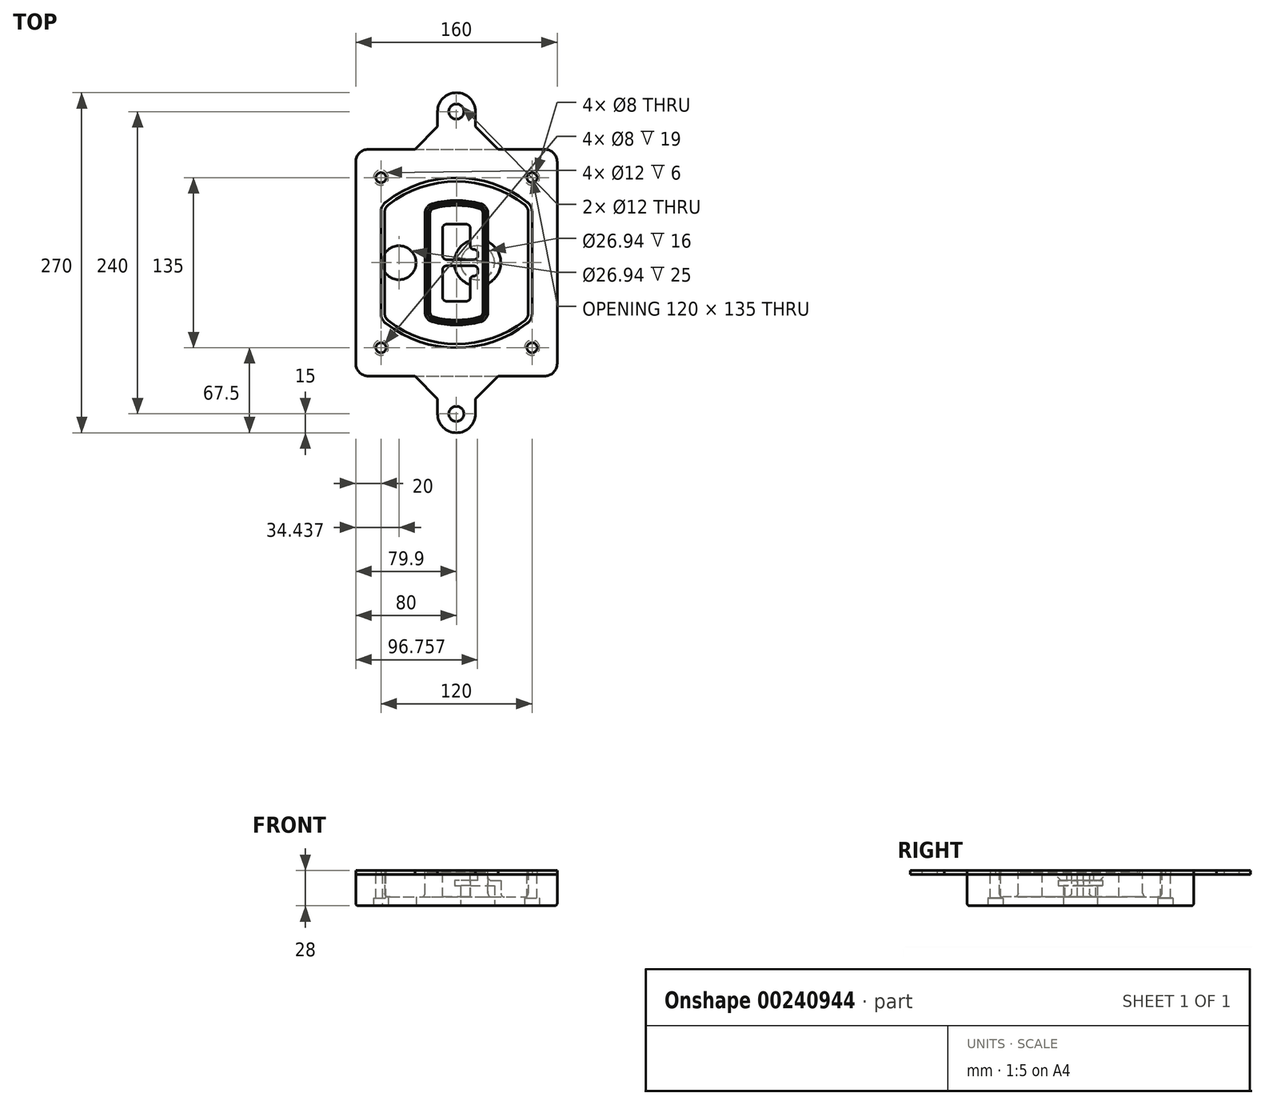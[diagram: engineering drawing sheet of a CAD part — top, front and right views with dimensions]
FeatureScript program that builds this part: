
annotation { "Feature Type Name" : "Feature", "Feature Type Description" : "" }
export const myFeature = defineFeature(function(context is Context, id is Id, definition is map)
    precondition{}
    {
        {
            var Q0;
            Q0=qCreatedBy(makeId("Top.planeOp"),FACE);
            var sketch = newSketch(context, id + "F0", { "sketchPlane" : qUnion([Q0])});
            skPoint(sketch, "E0.rect.middle", {"position": v(0, 0) * mm});
            skLineSegment(sketch, "E1.bottom", {"start": v(-70, -90) * mm, "end": v(70, -90) * mm});
            skLineSegment(sketch, "E1.top", {"start": v(-70, 90) * mm, "end": v(70, 90) * mm});
            skLineSegment(sketch, "E1.left", {"start": v(-80, -80) * mm, "end": v(-80, 80) * mm});
            skLineSegment(sketch, "E1.right", {"start": v(80, -80) * mm, "end": v(80, 80) * mm});
            skLineSegment(sketch, "E2", {"start": v(-80, 90) * mm, "end": v(80, -90) * mm, "construction": true});
            skLineSegment(sketch, "E3", {"start": v(80, 90) * mm, "end": v(-80, -90) * mm, "construction": true});
            skCircle(sketch, "E4", {"center": v(-60, 67.5) * mm, "radius": 4 * mm});
            skCircle(sketch, "E5", {"center": v(60, 67.5) * mm, "radius": 4 * mm});
            skCircle(sketch, "E6", {"center": v(60, -67.5) * mm, "radius": 4 * mm});
            skCircle(sketch, "E7", {"center": v(-60, -67.5) * mm, "radius": 4 * mm});
            skLineSegment(sketch, "E8", {"start": v(-60, 67.5) * mm, "end": v(60, 67.5) * mm, "construction": true});
            skLineSegment(sketch, "E9", {"start": v(60, 67.5) * mm, "end": v(60, -67.5) * mm, "construction": true});
            skLineSegment(sketch, "E10", {"start": v(60, -67.5) * mm, "end": v(-60, -67.5) * mm, "construction": true});
            skLineSegment(sketch, "E11", {"start": v(-60, -67.5) * mm, "end": v(-60, 67.5) * mm, "construction": true});
            skLineSegment(sketch, "E12", {"start": v(-60, 40.3) * mm, "end": v(-60, -40.3) * mm});
            skLineSegment(sketch, "E13", {"start": v(60, 40.3) * mm, "end": v(60, -40.3) * mm});
            skArc(sketch, "E14", {"start": v(56.15, 48.18) * mm, "mid": v(0, 67.5) * mm, "end": v(-56.15, 48.18) * mm});
            skArc(sketch, "E15", {"start": v(-56.15, -48.18) * mm, "mid": v(0, -67.5) * mm, "end": v(56.15, -48.18) * mm});
            skLineSegment(sketch, "E16", {"start": v(-60, 0) * mm, "end": v(60, 0) * mm, "construction": true});
            skPoint(sketch, "E17.visualSharp", {"position": v(-60, -45) * mm});
            skArc(sketch, "E17.filletArc", {"start": v(-60, -40.3) * mm, "mid": v(-58.99, -44.68) * mm, "end": v(-56.15, -48.18) * mm});
            skPoint(sketch, "E18.visualSharp", {"position": v(-60, 45) * mm});
            skArc(sketch, "E18.filletArc", {"start": v(-56.15, 48.18) * mm, "mid": v(-58.99, 44.68) * mm, "end": v(-60, 40.3) * mm});
            skPoint(sketch, "E19.visualSharp", {"position": v(60, 45) * mm});
            skArc(sketch, "E19.filletArc", {"start": v(60, 40.3) * mm, "mid": v(58.99, 44.68) * mm, "end": v(56.15, 48.18) * mm});
            skPoint(sketch, "E20.visualSharp", {"position": v(60, -45) * mm});
            skArc(sketch, "E20.filletArc", {"start": v(56.15, -48.18) * mm, "mid": v(58.99, -44.68) * mm, "end": v(60, -40.3) * mm});
            skPoint(sketch, "E21.visualSharp", {"position": v(-80, 90) * mm});
            skArc(sketch, "E21.filletArc", {"start": v(-70, 90) * mm, "mid": v(-77.07, 87.07) * mm, "end": v(-80, 80) * mm});
            skPoint(sketch, "E22.visualSharp", {"position": v(80, 90) * mm});
            skArc(sketch, "E22.filletArc", {"start": v(80, 80) * mm, "mid": v(77.07, 87.07) * mm, "end": v(70, 90) * mm});
            skPoint(sketch, "E23.visualSharp", {"position": v(80, -90) * mm});
            skArc(sketch, "E23.filletArc", {"start": v(70, -90) * mm, "mid": v(77.07, -87.07) * mm, "end": v(80, -80) * mm});
            skPoint(sketch, "E24.visualSharp", {"position": v(-80, -90) * mm});
            skArc(sketch, "E24.filletArc", {"start": v(-80, -80) * mm, "mid": v(-77.07, -87.07) * mm, "end": v(-70, -90) * mm});
            skArc(sketch, "E25.0", {"start": v(57, 40.3) * mm, "mid": v(56.3, 43.36) * mm, "end": v(54.3, 45.81) * mm});
            skLineSegment(sketch, "E25.1", {"start": v(57, 40.3) * mm, "end": v(57, -40.3) * mm});
            skArc(sketch, "E25.2", {"start": v(54.3, -45.81) * mm, "mid": v(56.3, -43.36) * mm, "end": v(57, -40.3) * mm});
            skArc(sketch, "E25.3", {"start": v(-54.3, -45.81) * mm, "mid": v(0, -64.5) * mm, "end": v(54.3, -45.81) * mm});
            skArc(sketch, "E25.4", {"start": v(-57, -40.3) * mm, "mid": v(-56.3, -43.36) * mm, "end": v(-54.3, -45.81) * mm});
            skArc(sketch, "E25.5", {"start": v(54.3, 45.81) * mm, "mid": v(0, 64.5) * mm, "end": v(-54.3, 45.81) * mm});
            skLineSegment(sketch, "E25.6", {"start": v(-57, 40.3) * mm, "end": v(-57, -40.3) * mm});
            skArc(sketch, "E25.7", {"start": v(-54.3, 45.81) * mm, "mid": v(-56.3, 43.36) * mm, "end": v(-57, 40.3) * mm});
            skArc(sketch, "E26.0", {"start": v(-58.62, 51.33) * mm, "mid": v(-62.58, 46.43) * mm, "end": v(-64, 40.3) * mm});
            skArc(sketch, "E26.1", {"start": v(58.62, 51.33) * mm, "mid": v(0, 71.5) * mm, "end": v(-58.62, 51.33) * mm});
            skArc(sketch, "E26.2", {"start": v(64, 40.3) * mm, "mid": v(62.58, 46.43) * mm, "end": v(58.62, 51.33) * mm});
            skLineSegment(sketch, "E26.3", {"start": v(64, 40.3) * mm, "end": v(64, -40.3) * mm});
            skArc(sketch, "E26.4", {"start": v(58.62, -51.33) * mm, "mid": v(62.58, -46.43) * mm, "end": v(64, -40.3) * mm});
            skLineSegment(sketch, "E26.5", {"start": v(-64, 40.3) * mm, "end": v(-64, -40.3) * mm});
            skArc(sketch, "E26.6", {"start": v(-58.62, -51.33) * mm, "mid": v(0, -71.5) * mm, "end": v(58.62, -51.33) * mm});
            skArc(sketch, "E26.7", {"start": v(-64, -40.3) * mm, "mid": v(-62.58, -46.43) * mm, "end": v(-58.62, -51.33) * mm});
            skSolve(sketch);
        }
        {
            var Q0;
            Q0=makeQuery(id+"F0.imprint","IMPRINT",FACE,{"disambiguationData":[TD([[makeQuery(id+"F0.imprint","IMPRINT",EDGE,{"derivedFrom":sQuery(id+"F0.wireOp",EDGE,"E1.bottom")}),1.0]])]});
            var Q1;
            Q1=makeQuery(id+"F0.imprint","IMPRINT",FACE,{"disambiguationData":[TD([[makeQuery(id+"F0.imprint","IMPRINT",EDGE,{"derivedFrom":sQuery(id+"F0.wireOp",EDGE,"E12")}),1.0]])]});
            var Q2;
            Q2=makeQuery(id+"F0.imprint","IMPRINT",FACE,{"disambiguationData":[TD([[makeQuery(id+"F0.imprint","IMPRINT",EDGE,{"derivedFrom":sQuery(id+"F0.wireOp",EDGE,"E25.0")}),1.0]])]});
            var Q3;
            Q3=makeQuery(id+"F0.imprint","IMPRINT",FACE,{"disambiguationData":[TD([[makeQuery(id+"F0.imprint","IMPRINT",EDGE,{"derivedFrom":sQuery(id+"F0.wireOp",EDGE,"E12")}),-1.0]])]});
            extrude(context, id + "F1", {"entities" : qUnion([Q0, Q1, Q2, Q3]), "oppositeDirection" : true, "depth" : 25 * mm});
        }
        {
            var Q0;
            Q0=makeQuery(id+"F0.imprint","IMPRINT",FACE,{"disambiguationData":[TD([[makeQuery(id+"F0.imprint","IMPRINT",EDGE,{"derivedFrom":sQuery(id+"F0.wireOp",EDGE,"E12")}),1.0]])]});
            extrude(context, id + "F2", {"entities" : qUnion([Q0]), "operationType" : NewBodyOperationType.ADD, "depth" : 3 * mm});
        }
        {
            var Q0;
            Q0=makeQuery(id+"F0.imprint","IMPRINT",FACE,{"disambiguationData":[TD([[makeQuery(id+"F0.imprint","IMPRINT",EDGE,{"derivedFrom":sQuery(id+"F0.wireOp",EDGE,"E25.0")}),1.0]])]});
            extrude(context, id + "F3", {"entities" : qUnion([Q0]), "operationType" : NewBodyOperationType.REMOVE, "oppositeDirection" : true, "depth" : 18 * mm});
        }
        {
            var Q0;
            Q0=makeQuery(id+"F2.opExtrude","CAP_FACE",FACE,{"disambiguationData":[OSD([sQuery(id+"F0.wireOp",EDGE,"E12"),sQuery(id+"F0.wireOp",EDGE,"E13"),sQuery(id+"F0.wireOp",EDGE,"E14"),sQuery(id+"F0.wireOp",EDGE,"E15"),sQuery(id+"F0.wireOp",EDGE,"E17.filletArc"),sQuery(id+"F0.wireOp",EDGE,"E18.filletArc"),sQuery(id+"F0.wireOp",EDGE,"E19.filletArc"),sQuery(id+"F0.wireOp",EDGE,"E20.filletArc"),sQuery(id+"F0.wireOp",EDGE,"E25.0"),sQuery(id+"F0.wireOp",EDGE,"E25.1"),sQuery(id+"F0.wireOp",EDGE,"E25.2"),sQuery(id+"F0.wireOp",EDGE,"E25.3"),sQuery(id+"F0.wireOp",EDGE,"E25.4"),sQuery(id+"F0.wireOp",EDGE,"E25.5"),sQuery(id+"F0.wireOp",EDGE,"E25.6"),sQuery(id+"F0.wireOp",EDGE,"E25.7")])],"isStart":false});
            var sketch = newSketch(context, id + "F4", { "sketchPlane" : qUnion([Q0])});
            skArc(sketch, "E27.0", {"start": v(-19.08, -46.97) * mm, "mid": v(0, -49.5) * mm, "end": v(19.08, -46.97) * mm});
            skArc(sketch, "E28.0", {"start": v(19.08, 46.97) * mm, "mid": v(0, 49.5) * mm, "end": v(-19.08, 46.97) * mm});
            skLineSegment(sketch, "E29", {"start": v(-25, 39.25) * mm, "end": v(-25, -39.25) * mm});
            skLineSegment(sketch, "E30", {"start": v(25, 39.25) * mm, "end": v(25, -39.25) * mm});
            skLineSegment(sketch, "E31", {"start": v(-25, 45.1) * mm, "end": v(25, 45.1) * mm, "construction": true});
            skLineSegment(sketch, "E32", {"start": v(-25, -45.1) * mm, "end": v(25, -45.1) * mm, "construction": true});
            skPoint(sketch, "E33.visualSharp", {"position": v(-25, 45.1) * mm});
            skArc(sketch, "E33.filletArc", {"start": v(-19.08, 46.97) * mm, "mid": v(-23.35, 44.11) * mm, "end": v(-25, 39.25) * mm});
            skPoint(sketch, "E34.visualSharp", {"position": v(25, 45.1) * mm});
            skArc(sketch, "E34.filletArc", {"start": v(25, 39.25) * mm, "mid": v(23.35, 44.11) * mm, "end": v(19.08, 46.97) * mm});
            skPoint(sketch, "E35.visualSharp", {"position": v(25, -45.1) * mm});
            skArc(sketch, "E35.filletArc", {"start": v(19.08, -46.97) * mm, "mid": v(23.35, -44.11) * mm, "end": v(25, -39.25) * mm});
            skPoint(sketch, "E36.visualSharp", {"position": v(-25, -45.1) * mm});
            skArc(sketch, "E36.filletArc", {"start": v(-25, -39.25) * mm, "mid": v(-23.35, -44.11) * mm, "end": v(-19.08, -46.97) * mm});
            skArc(sketch, "E37.0", {"start": v(54.3, 45.81) * mm, "mid": v(0, 64.5) * mm, "end": v(-54.3, 45.81) * mm});
            skArc(sketch, "E37.1", {"start": v(-54.3, 45.81) * mm, "mid": v(-56.3, 43.36) * mm, "end": v(-57, 40.3) * mm});
            skLineSegment(sketch, "E37.2", {"start": v(-57, 40.3) * mm, "end": v(-57, -40.3) * mm});
            skArc(sketch, "E37.3", {"start": v(-57, -40.3) * mm, "mid": v(-56.3, -43.36) * mm, "end": v(-54.3, -45.81) * mm});
            skArc(sketch, "E37.4", {"start": v(-54.3, -45.81) * mm, "mid": v(0, -64.5) * mm, "end": v(54.3, -45.81) * mm});
            skArc(sketch, "E37.5", {"start": v(54.3, -45.81) * mm, "mid": v(56.3, -43.36) * mm, "end": v(57, -40.3) * mm});
            skLineSegment(sketch, "E37.6", {"start": v(57, 40.3) * mm, "end": v(57, -40.3) * mm});
            skArc(sketch, "E37.7", {"start": v(57, 40.3) * mm, "mid": v(56.3, 43.36) * mm, "end": v(54.3, 45.81) * mm});
            skLineSegment(sketch, "E38.0", {"start": v(23, 39.25) * mm, "end": v(23, -39.25) * mm});
            skArc(sketch, "E38.1", {"start": v(18.56, -45.04) * mm, "mid": v(21.76, -42.9) * mm, "end": v(23, -39.25) * mm});
            skArc(sketch, "E38.2", {"start": v(-18.56, -45.04) * mm, "mid": v(0, -47.5) * mm, "end": v(18.56, -45.04) * mm});
            skArc(sketch, "E38.3", {"start": v(-23, -39.25) * mm, "mid": v(-21.76, -42.9) * mm, "end": v(-18.56, -45.04) * mm});
            skLineSegment(sketch, "E38.4", {"start": v(-23, 39.25) * mm, "end": v(-23, -39.25) * mm});
            skArc(sketch, "E38.5", {"start": v(23, 39.25) * mm, "mid": v(21.76, 42.9) * mm, "end": v(18.56, 45.04) * mm});
            skArc(sketch, "E38.6", {"start": v(-18.56, 45.04) * mm, "mid": v(-21.76, 42.9) * mm, "end": v(-23, 39.25) * mm});
            skArc(sketch, "E38.7", {"start": v(18.56, 45.04) * mm, "mid": v(0, 47.5) * mm, "end": v(-18.56, 45.04) * mm});
            skArc(sketch, "E39.0", {"start": v(21, 39.25) * mm, "mid": v(20.18, 41.68) * mm, "end": v(18.04, 43.1) * mm});
            skLineSegment(sketch, "E39.1", {"start": v(21, 39.25) * mm, "end": v(21, -39.25) * mm});
            skArc(sketch, "E39.2", {"start": v(18.04, -43.1) * mm, "mid": v(20.18, -41.68) * mm, "end": v(21, -39.25) * mm});
            skArc(sketch, "E39.3", {"start": v(-18.04, -43.1) * mm, "mid": v(0, -45.5) * mm, "end": v(18.04, -43.1) * mm});
            skArc(sketch, "E39.4", {"start": v(-21, -39.25) * mm, "mid": v(-20.18, -41.68) * mm, "end": v(-18.04, -43.1) * mm});
            skArc(sketch, "E39.5", {"start": v(18.04, 43.1) * mm, "mid": v(0, 45.5) * mm, "end": v(-18.04, 43.1) * mm});
            skLineSegment(sketch, "E39.6", {"start": v(-21, 39.25) * mm, "end": v(-21, -39.25) * mm});
            skArc(sketch, "E39.7", {"start": v(-18.04, 43.1) * mm, "mid": v(-20.18, 41.68) * mm, "end": v(-21, 39.25) * mm});
            skLineSegment(sketch, "E40", {"start": v(-25, 0) * mm, "end": v(25, 0) * mm, "construction": true});
            skLineSegment(sketch, "E41", {"start": v(-11, 5.5) * mm, "end": v(-11, 27.5) * mm});
            skLineSegment(sketch, "E42", {"start": v(-8, 30.5) * mm, "end": v(8, 30.5) * mm});
            skLineSegment(sketch, "E43", {"start": v(11, 27.5) * mm, "end": v(11, 13.5) * mm});
            skLineSegment(sketch, "E44", {"start": v(14, 10.5) * mm, "end": v(14, 10.5) * mm});
            skLineSegment(sketch, "E45", {"start": v(17, 7.5) * mm, "end": v(17, 5.5) * mm});
            skLineSegment(sketch, "E46", {"start": v(14, 2.5) * mm, "end": v(-8, 2.5) * mm});
            skPoint(sketch, "E47.visualSharp", {"position": v(-11, 30.5) * mm});
            skArc(sketch, "E47.filletArc", {"start": v(-8, 30.5) * mm, "mid": v(-10.12, 29.62) * mm, "end": v(-11, 27.5) * mm});
            skPoint(sketch, "E48.visualSharp", {"position": v(11, 30.5) * mm});
            skArc(sketch, "E48.filletArc", {"start": v(11, 27.5) * mm, "mid": v(10.12, 29.62) * mm, "end": v(8, 30.5) * mm});
            skPoint(sketch, "E49.visualSharp", {"position": v(11, 10.5) * mm});
            skArc(sketch, "E49.filletArc", {"start": v(11, 13.5) * mm, "mid": v(11.88, 11.38) * mm, "end": v(14, 10.5) * mm});
            skPoint(sketch, "E50.visualSharp", {"position": v(17, 10.5) * mm});
            skArc(sketch, "E50.filletArc", {"start": v(17, 7.5) * mm, "mid": v(16.12, 9.62) * mm, "end": v(14, 10.5) * mm});
            skPoint(sketch, "E51.visualSharp", {"position": v(17, 2.5) * mm});
            skArc(sketch, "E51.filletArc", {"start": v(14, 2.5) * mm, "mid": v(16.12, 3.38) * mm, "end": v(17, 5.5) * mm});
            skPoint(sketch, "E52.visualSharp", {"position": v(-11, 2.5) * mm});
            skArc(sketch, "E52.filletArc", {"start": v(-11, 5.5) * mm, "mid": v(-10.12, 3.38) * mm, "end": v(-8, 2.5) * mm});
            skLineSegment(sketch, "E53.0.MirrorCS", {"start": v(14, -2.5) * mm, "end": v(-8, -2.5) * mm});
            skArc(sketch, "E54.0.MirrorCS", {"start": v(-11, -5.5) * mm, "mid": v(-10.12, -3.38) * mm, "end": v(-8, -2.5) * mm});
            skLineSegment(sketch, "E55.0.MirrorCS", {"start": v(-11, -5.5) * mm, "end": v(-11, -27.5) * mm});
            skArc(sketch, "E56.0.MirrorCS", {"start": v(-8, -30.5) * mm, "mid": v(-10.12, -29.62) * mm, "end": v(-11, -27.5) * mm});
            skLineSegment(sketch, "E57.0.MirrorCS", {"start": v(-8, -30.5) * mm, "end": v(8, -30.5) * mm});
            skArc(sketch, "E58.0.MirrorCS", {"start": v(11, -27.5) * mm, "mid": v(10.12, -29.62) * mm, "end": v(8, -30.5) * mm});
            skLineSegment(sketch, "E59.0.MirrorCS", {"start": v(11, -27.5) * mm, "end": v(11, -13.5) * mm});
            skArc(sketch, "E60.0.MirrorCS", {"start": v(11, -13.5) * mm, "mid": v(11.88, -11.38) * mm, "end": v(14, -10.5) * mm});
            skArc(sketch, "E61.0.MirrorCS", {"start": v(17, -7.5) * mm, "mid": v(16.12, -9.62) * mm, "end": v(14, -10.5) * mm});
            skLineSegment(sketch, "E62.0.MirrorCS", {"start": v(17, -7.5) * mm, "end": v(17, -5.5) * mm});
            skArc(sketch, "E63.0.MirrorCS", {"start": v(14, -2.5) * mm, "mid": v(16.12, -3.38) * mm, "end": v(17, -5.5) * mm});
            skSolve(sketch);
        }
        {
            var Q0;
            Q0=makeQuery(id+"F4.imprint","IMPRINT",FACE,{"disambiguationData":[TD([[makeQuery(id+"F4.imprint","IMPRINT",EDGE,{"derivedFrom":sQuery(id+"F4.wireOp",EDGE,"E27.0")}),1.0]])]});
            var Q1;
            Q1=makeQuery(id+"F4.imprint","IMPRINT",FACE,{"disambiguationData":[TD([[makeQuery(id+"F4.imprint","IMPRINT",EDGE,{"derivedFrom":sQuery(id+"F4.wireOp",EDGE,"E38.0")}),-1.0]])]});
            var Q2;
            Q2=makeQuery(id+"F4.imprint","IMPRINT",FACE,{"disambiguationData":[TD([[makeQuery(id+"F4.imprint","IMPRINT",EDGE,{"derivedFrom":sQuery(id+"F4.wireOp",EDGE,"E39.0")}),1.0]])]});
            extrude(context, id + "F5", {"entities" : qUnion([Q0, Q1, Q2]), "operationType" : NewBodyOperationType.ADD, "endBound" : BoundingType.UP_TO_NEXT, "oppositeDirection" : true, "depth" : 25 * mm});
        }
        {
            var Q0;
            Q0=makeQuery(id+"F4.imprint","IMPRINT",FACE,{"disambiguationData":[TD([[makeQuery(id+"F4.imprint","IMPRINT",EDGE,{"derivedFrom":sQuery(id+"F4.wireOp",EDGE,"E38.0")}),-1.0]])]});
            extrude(context, id + "F6", {"entities" : qUnion([Q0]), "operationType" : NewBodyOperationType.REMOVE, "oppositeDirection" : true, "depth" : 2 * mm});
        }
        {
            var Q0;
            Q0=makeQuery(id+"F1.opExtrude","CAP_FACE",FACE,{"disambiguationData":[OSD([sQuery(id+"F0.wireOp",EDGE,"E1.bottom"),sQuery(id+"F0.wireOp",EDGE,"E1.top"),sQuery(id+"F0.wireOp",EDGE,"E1.left"),sQuery(id+"F0.wireOp",EDGE,"E1.right"),sQuery(id+"F0.wireOp",EDGE,"E4"),sQuery(id+"F0.wireOp",EDGE,"E5"),sQuery(id+"F0.wireOp",EDGE,"E6"),sQuery(id+"F0.wireOp",EDGE,"E7"),sQuery(id+"F0.wireOp",EDGE,"E21.filletArc"),sQuery(id+"F0.wireOp",EDGE,"E22.filletArc"),sQuery(id+"F0.wireOp",EDGE,"E23.filletArc"),sQuery(id+"F0.wireOp",EDGE,"E24.filletArc")])],"isStart":false});
            var sketch = newSketch(context, id + "F7", { "sketchPlane" : qUnion([Q0])});
            skCircle(sketch, "E64", {"center": v(16.76, 0) * mm, "radius": 13.47 * mm});
            skCircle(sketch, "E65", {"center": v(-45.56, 0) * mm, "radius": 13.47 * mm});
            skLineSegment(sketch, "E66", {"start": v(80, 0) * mm, "end": v(-80, 0) * mm});
            skCircle(sketch, "E67", {"center": v(16.76, 0) * mm, "radius": 18.47 * mm});
            skCircle(sketch, "E68", {"center": v(60, -67.5) * mm, "radius": 6 * mm});
            skCircle(sketch, "E69", {"center": v(-60, -67.5) * mm, "radius": 6 * mm});
            skCircle(sketch, "E70", {"center": v(-60, 67.5) * mm, "radius": 6 * mm});
            skCircle(sketch, "E71", {"center": v(60, 67.5) * mm, "radius": 6 * mm});
            skSolve(sketch);
        }
        {
            var Q0;
            {var subQ1=sQuery(id+"F7.wireOp",EDGE,"E66");var subQ4=sQuery(id+"F7.wireOp",EDGE,"E64");var subQ6=makeQuery(id+"F7.imprint","INTERSECT",VERTEX,{"disambiguationData":[OD(0.0)],"derivedFrom":[subQ4,subQ1]});Q0=makeQuery(id+"F7.imprint","IMPRINT",FACE,{"disambiguationData":[TD([[makeQuery(id+"F7.imprint","IMPRINT",EDGE,{"disambiguationData":[TD([[subQ6,-1.0]])],"derivedFrom":subQ4}),-1.0]])]});}
            var Q1;
            {var subQ0=sQuery(id+"F7.wireOp",EDGE,"E66");var subQ1=sQuery(id+"F7.wireOp",EDGE,"E64");var subQ3=makeQuery(id+"F7.imprint","INTERSECT",VERTEX,{"disambiguationData":[OD(0.0)],"derivedFrom":[subQ1,subQ0]});Q1=makeQuery(id+"F7.imprint","IMPRINT",FACE,{"disambiguationData":[TD([[makeQuery(id+"F7.imprint","IMPRINT",EDGE,{"disambiguationData":[TD([[subQ3,-1.0]])],"derivedFrom":subQ1}),1.0]])]});}
            var Q2;
            {var subQ0=sQuery(id+"F7.wireOp",EDGE,"E66");var subQ1=sQuery(id+"F7.wireOp",EDGE,"E64");var subQ3=makeQuery(id+"F7.imprint","INTERSECT",VERTEX,{"disambiguationData":[OD(0.0)],"derivedFrom":[subQ1,subQ0]});Q2=makeQuery(id+"F7.imprint","IMPRINT",FACE,{"disambiguationData":[TD([[makeQuery(id+"F7.imprint","IMPRINT",EDGE,{"disambiguationData":[TD([[subQ3,1.0]])],"derivedFrom":subQ1}),1.0]])]});}
            var Q3;
            {var subQ1=sQuery(id+"F7.wireOp",EDGE,"E66");var subQ4=sQuery(id+"F7.wireOp",EDGE,"E64");var subQ6=makeQuery(id+"F7.imprint","INTERSECT",VERTEX,{"disambiguationData":[OD(0.0)],"derivedFrom":[subQ4,subQ1]});Q3=makeQuery(id+"F7.imprint","IMPRINT",FACE,{"disambiguationData":[TD([[makeQuery(id+"F7.imprint","IMPRINT",EDGE,{"disambiguationData":[TD([[subQ6,1.0]])],"derivedFrom":subQ4}),-1.0]])]});}
            extrude(context, id + "F8", {"entities" : qUnion([Q0, Q1, Q2, Q3]), "operationType" : NewBodyOperationType.ADD, "oppositeDirection" : true, "depth" : 20 * mm});
        }
        {
            var Q0;
            {var subQ0=sQuery(id+"F7.wireOp",EDGE,"E66");var subQ1=sQuery(id+"F7.wireOp",EDGE,"E64");var subQ3=makeQuery(id+"F7.imprint","INTERSECT",VERTEX,{"disambiguationData":[OD(0.0)],"derivedFrom":[subQ1,subQ0]});Q0=makeQuery(id+"F7.imprint","IMPRINT",FACE,{"disambiguationData":[TD([[makeQuery(id+"F7.imprint","IMPRINT",EDGE,{"disambiguationData":[TD([[subQ3,-1.0]])],"derivedFrom":subQ1}),1.0]])]});}
            var Q1;
            {var subQ0=sQuery(id+"F7.wireOp",EDGE,"E66");var subQ1=sQuery(id+"F7.wireOp",EDGE,"E64");var subQ3=makeQuery(id+"F7.imprint","INTERSECT",VERTEX,{"disambiguationData":[OD(0.0)],"derivedFrom":[subQ1,subQ0]});Q1=makeQuery(id+"F7.imprint","IMPRINT",FACE,{"disambiguationData":[TD([[makeQuery(id+"F7.imprint","IMPRINT",EDGE,{"disambiguationData":[TD([[subQ3,1.0]])],"derivedFrom":subQ1}),1.0]])]});}
            extrude(context, id + "F9", {"entities" : qUnion([Q0, Q1]), "operationType" : NewBodyOperationType.REMOVE, "oppositeDirection" : true, "depth" : 16 * mm});
        }
        {
            var Q0;
            {var subQ0=sQuery(id+"F7.wireOp",EDGE,"E66");var subQ1=sQuery(id+"F7.wireOp",EDGE,"E65");var subQ3=makeQuery(id+"F7.imprint","INTERSECT",VERTEX,{"disambiguationData":[OD(0.0)],"derivedFrom":[subQ1,subQ0]});Q0=makeQuery(id+"F7.imprint","IMPRINT",FACE,{"disambiguationData":[TD([[makeQuery(id+"F7.imprint","IMPRINT",EDGE,{"disambiguationData":[TD([[subQ3,-1.0]])],"derivedFrom":subQ1}),1.0]])]});}
            var Q1;
            {var subQ0=sQuery(id+"F7.wireOp",EDGE,"E66");var subQ1=sQuery(id+"F7.wireOp",EDGE,"E65");var subQ3=makeQuery(id+"F7.imprint","INTERSECT",VERTEX,{"disambiguationData":[OD(0.0)],"derivedFrom":[subQ1,subQ0]});Q1=makeQuery(id+"F7.imprint","IMPRINT",FACE,{"disambiguationData":[TD([[makeQuery(id+"F7.imprint","IMPRINT",EDGE,{"disambiguationData":[TD([[subQ3,1.0]])],"derivedFrom":subQ1}),1.0]])]});}
            extrude(context, id + "F10", {"entities" : qUnion([Q0, Q1]), "operationType" : NewBodyOperationType.REMOVE, "oppositeDirection" : true, "depth" : 25 * mm});
        }
        {
            var Q0;
            Q0=makeQuery(id+"F7.imprint","IMPRINT",FACE,{"disambiguationData":[TD([[makeQuery(id+"F7.imprint","IMPRINT",EDGE,{"derivedFrom":sQuery(id+"F7.wireOp",EDGE,"E68")}),1.0]])]});
            var Q1;
            Q1=makeQuery(id+"F7.imprint","IMPRINT",FACE,{"disambiguationData":[TD([[makeQuery(id+"F7.imprint","IMPRINT",EDGE,{"derivedFrom":makeQuery(id+"F1.opExtrude","CAP_EDGE",EDGE,{"disambiguationData":[OSD([sQuery(id+"F0.wireOp",EDGE,"E5")])],"isStart":false})}),-1.0]])]});
            var Q2;
            Q2=makeQuery(id+"F7.imprint","IMPRINT",FACE,{"disambiguationData":[TD([[makeQuery(id+"F7.imprint","IMPRINT",EDGE,{"derivedFrom":sQuery(id+"F7.wireOp",EDGE,"E69")}),1.0]])]});
            var Q3;
            Q3=makeQuery(id+"F7.imprint","IMPRINT",FACE,{"disambiguationData":[TD([[makeQuery(id+"F7.imprint","IMPRINT",EDGE,{"derivedFrom":makeQuery(id+"F1.opExtrude","CAP_EDGE",EDGE,{"disambiguationData":[OSD([sQuery(id+"F0.wireOp",EDGE,"E4")])],"isStart":false})}),-1.0]])]});
            var Q4;
            Q4=makeQuery(id+"F7.imprint","IMPRINT",FACE,{"disambiguationData":[TD([[makeQuery(id+"F7.imprint","IMPRINT",EDGE,{"derivedFrom":sQuery(id+"F7.wireOp",EDGE,"E70")}),1.0]])]});
            var Q5;
            Q5=makeQuery(id+"F7.imprint","IMPRINT",FACE,{"disambiguationData":[TD([[makeQuery(id+"F7.imprint","IMPRINT",EDGE,{"derivedFrom":makeQuery(id+"F1.opExtrude","CAP_EDGE",EDGE,{"disambiguationData":[OSD([sQuery(id+"F0.wireOp",EDGE,"E7")])],"isStart":false})}),-1.0]])]});
            var Q6;
            Q6=makeQuery(id+"F7.imprint","IMPRINT",FACE,{"disambiguationData":[TD([[makeQuery(id+"F7.imprint","IMPRINT",EDGE,{"derivedFrom":sQuery(id+"F7.wireOp",EDGE,"E71")}),1.0]])]});
            var Q7;
            Q7=makeQuery(id+"F7.imprint","IMPRINT",FACE,{"disambiguationData":[TD([[makeQuery(id+"F7.imprint","IMPRINT",EDGE,{"derivedFrom":makeQuery(id+"F1.opExtrude","CAP_EDGE",EDGE,{"disambiguationData":[OSD([sQuery(id+"F0.wireOp",EDGE,"E6")])],"isStart":false})}),-1.0]])]});
            extrude(context, id + "F11", {"entities" : qUnion([Q0, Q1, Q2, Q3, Q4, Q5, Q6, Q7]), "operationType" : NewBodyOperationType.REMOVE, "oppositeDirection" : true, "depth" : 6 * mm});
        }
        {
            var Q0;
            Q0=makeQuery(id+"F9.boolean.opBoolean","COPY",FACE,{"derivedFrom":makeQuery(id+"F9.opExtrude","CAP_FACE",FACE,{"disambiguationData":[OSD([sQuery(id+"F7.wireOp",EDGE,"E64")])],"isStart":false})});
            var sketch = newSketch(context, id + "F12", { "sketchPlane" : qUnion([Q0])});
            skArc(sketch, "E72.0", {"start": v(11, 17.55) * mm, "mid": v(2.57, 11.82) * mm, "end": v(-1.54, 2.5) * mm});
            skArc(sketch, "E72.1", {"start": v(-1.54, -2.5) * mm, "mid": v(2.57, -11.82) * mm, "end": v(11, -17.55) * mm});
            skLineSegment(sketch, "E73", {"start": v(-1.54, -2.5) * mm, "end": v(14, -2.5) * mm});
            skLineSegment(sketch, "E74.0", {"start": v(14, 2.5) * mm, "end": v(-1.54, 2.5) * mm});
            skArc(sketch, "E74.1", {"start": v(14, 2.5) * mm, "mid": v(16.12, 3.38) * mm, "end": v(17, 5.5) * mm});
            skLineSegment(sketch, "E74.2", {"start": v(17, 7.5) * mm, "end": v(17, 5.5) * mm});
            skArc(sketch, "E74.3", {"start": v(17, 7.5) * mm, "mid": v(16.12, 9.62) * mm, "end": v(14, 10.5) * mm});
            skArc(sketch, "E74.4", {"start": v(11, 13.5) * mm, "mid": v(11.88, 11.38) * mm, "end": v(14, 10.5) * mm});
            skLineSegment(sketch, "E74.5", {"start": v(11, 17.55) * mm, "end": v(11, 13.5) * mm});
            skLineSegment(sketch, "E74.7", {"start": v(14, -2.5) * mm, "end": v(-1.54, -2.5) * mm});
            skArc(sketch, "E74.8", {"start": v(14, -2.5) * mm, "mid": v(16.12, -3.38) * mm, "end": v(17, -5.5) * mm});
            skLineSegment(sketch, "E74.9", {"start": v(17, -7.5) * mm, "end": v(17, -5.5) * mm});
            skArc(sketch, "E74.10", {"start": v(17, -7.5) * mm, "mid": v(16.12, -9.62) * mm, "end": v(14, -10.5) * mm});
            skArc(sketch, "E74.11", {"start": v(11, -13.5) * mm, "mid": v(11.88, -11.38) * mm, "end": v(14, -10.5) * mm});
            skLineSegment(sketch, "E74.12", {"start": v(11, -17.55) * mm, "end": v(11, -13.5) * mm});
            skPoint(sketch, "E75.orphan", {"position": v(11, -27.5) * mm});
            skPoint(sketch, "E76.orphan", {"position": v(-8, -2.5) * mm});
            skPoint(sketch, "E77.orphan", {"position": v(-8, 2.5) * mm});
            skPoint(sketch, "E78.orphan", {"position": v(11, 27.5) * mm});
            skSolve(sketch);
        }
        {
            var Q0;
            {var subQ7=sQuery(id+"F12.wireOp",EDGE,"E72.0");var subQ14=sQuery(id+"F12.wireOp",EDGE,"E72.1");var subQ16=sQuery(id+"F12.wireOp",EDGE,"E74.1");var subQ18=sQuery(id+"F12.wireOp",EDGE,"E74.8");Q0=qUnion([makeQuery(id+"F12.imprint","IMPRINT",FACE,{"disambiguationData":[TD([[makeQuery(id+"F12.imprint","IMPRINT",EDGE,{"derivedFrom":subQ7}),1.0]])]}),makeQuery(id+"F12.imprint","IMPRINT",FACE,{"disambiguationData":[TD([[makeQuery(id+"F12.imprint","IMPRINT",EDGE,{"derivedFrom":subQ14}),1.0]])]}),makeQuery(id+"F12.imprint","IMPRINT",FACE,{"disambiguationData":[TD([[makeQuery(id+"F12.imprint","IMPRINT",EDGE,{"derivedFrom":subQ16}),1.0]])]}),makeQuery(id+"F12.imprint","IMPRINT",FACE,{"disambiguationData":[TD([[makeQuery(id+"F12.imprint","IMPRINT",EDGE,{"derivedFrom":subQ18}),-1.0]])]})]);}
            var Q1;
            Q1=makeQuery(id+"F5.boolean.opBoolean","SPLIT",FACE,{"disambiguationData":[TD([makeQuery(id+"F5.opExtrude","SWEPT_FACE",FACE,{"disambiguationData":[OSD([sQuery(id+"F4.wireOp",EDGE,"E41")])]})])],"derivedFrom":makeQuery(id+"F3.boolean.opBoolean","COPY",FACE,{"derivedFrom":makeQuery(id+"F3.opExtrude","CAP_FACE",FACE,{"disambiguationData":[OSD([sQuery(id+"F0.wireOp",EDGE,"E25.0"),sQuery(id+"F0.wireOp",EDGE,"E25.1"),sQuery(id+"F0.wireOp",EDGE,"E25.2"),sQuery(id+"F0.wireOp",EDGE,"E25.3"),sQuery(id+"F0.wireOp",EDGE,"E25.4"),sQuery(id+"F0.wireOp",EDGE,"E25.5"),sQuery(id+"F0.wireOp",EDGE,"E25.6"),sQuery(id+"F0.wireOp",EDGE,"E25.7")])],"isStart":false})})});
            extrude(context, id + "F13", {"entities" : qUnion([Q0]), "operationType" : NewBodyOperationType.REMOVE, "endBound" : BoundingType.UP_TO_SURFACE, "endBoundEntityFace" : qUnion([Q1]), "depth" : 25 * mm});
        }
        {
            var Q0;
            Q0=makeQuery(id+"F3.boolean.opBoolean","COPY",EDGE,{"derivedFrom":makeQuery(id+"F3.opExtrude","CAP_EDGE",EDGE,{"disambiguationData":[OSD([sQuery(id+"F0.wireOp",EDGE,"E25.6")])],"isStart":false})});
            var Q1;
            Q1=makeQuery(id+"F8.boolean.opBoolean","INTERSECT",EDGE,{"derivedFrom":[makeQuery(id+"F5.opExtrude","SWEPT_FACE",FACE,{"disambiguationData":[OSD([sQuery(id+"F4.wireOp",EDGE,"E30")])]}),makeQuery(id+"F8.opExtrude","CAP_FACE",FACE,{"disambiguationData":[OSD([sQuery(id+"F7.wireOp",EDGE,"E67")])],"isStart":false})]});
            var Q2;
            Q2=makeQuery(id+"F8.boolean.opBoolean","INTERSECT",EDGE,{"disambiguationData":[OD(1.0)],"derivedFrom":[makeQuery(id+"F5.opExtrude","SWEPT_FACE",FACE,{"disambiguationData":[OSD([sQuery(id+"F4.wireOp",EDGE,"E30")])]}),makeQuery(id+"F8.opExtrude","SWEPT_FACE",FACE,{"disambiguationData":[OSD([sQuery(id+"F7.wireOp",EDGE,"E67")])]})]});
            var Q3;
            {var subQ0=sQuery(id+"F4.wireOp",EDGE,"E30");Q3=makeQuery(id+"F8.boolean.opBoolean","SPLIT",EDGE,{"disambiguationData":[TD([makeQuery(id+"F5.opExtrude","SWEPT_FACE",FACE,{"disambiguationData":[OSD([sQuery(id+"F4.wireOp",EDGE,"E35.filletArc")])]})])],"derivedFrom":makeQuery(id+"F5.opExtrude","CAP_EDGE",EDGE,{"disambiguationData":[OSD([subQ0])],"isStart":false})});}
            var Q4;
            {var subQ0=sQuery(id+"F0.wireOp",EDGE,"E25.7");var subQ1=sQuery(id+"F0.wireOp",EDGE,"E25.1");var subQ2=sQuery(id+"F0.wireOp",EDGE,"E25.6");var subQ3=sQuery(id+"F0.wireOp",EDGE,"E25.5");var subQ4=sQuery(id+"F0.wireOp",EDGE,"E25.4");var subQ5=sQuery(id+"F0.wireOp",EDGE,"E25.0");var subQ6=sQuery(id+"F0.wireOp",EDGE,"E25.2");var subQ7=sQuery(id+"F0.wireOp",EDGE,"E25.3");Q4=makeQuery(id+"F8.boolean.opBoolean","INTERSECT",EDGE,{"derivedFrom":[makeQuery(id+"F5.boolean.opBoolean","SPLIT",FACE,{"disambiguationData":[TD([makeQuery(id+"F2.opExtrude","SWEPT_FACE",FACE,{"disambiguationData":[OSD([subQ5])]})])],"derivedFrom":makeQuery(id+"F3.boolean.opBoolean","COPY",FACE,{"derivedFrom":makeQuery(id+"F3.opExtrude","CAP_FACE",FACE,{"disambiguationData":[OSD([subQ5,subQ1,subQ6,subQ7,subQ4,subQ3,subQ2,subQ0])],"isStart":false})})}),makeQuery(id+"F8.opExtrude","SWEPT_FACE",FACE,{"disambiguationData":[OSD([sQuery(id+"F7.wireOp",EDGE,"E67")])]})]});}
            var Q5;
            Q5=makeQuery(id+"F8.boolean.opBoolean","INTERSECT",EDGE,{"disambiguationData":[OD(0.0)],"derivedFrom":[makeQuery(id+"F5.opExtrude","SWEPT_FACE",FACE,{"disambiguationData":[OSD([sQuery(id+"F4.wireOp",EDGE,"E30")])]}),makeQuery(id+"F8.opExtrude","SWEPT_FACE",FACE,{"disambiguationData":[OSD([sQuery(id+"F7.wireOp",EDGE,"E67")])]})]});
            fillet(context, id + "F14", {"entities" : qUnion([Q0, Q1, Q2, Q3, Q4, Q5]), "radius" : 3 * mm, "tangentPropagation" : true, "allowEdgeOverflow" : false});
        }
        {
            var Q0;
            Q0=makeQuery(id+"F1.opExtrude","CAP_EDGE",EDGE,{"disambiguationData":[OSD([sQuery(id+"F0.wireOp",EDGE,"E1.bottom")])],"isStart":false});
            fillet(context, id + "F15", {"entities" : qUnion([Q0]), "radius" : 2 * mm, "tangentPropagation" : true, "allowEdgeOverflow" : false});
        }
        {
            var Q0;
            {var subQ0=sQuery(id+"F0.wireOp",EDGE,"E22.filletArc");var subQ1=sQuery(id+"F0.wireOp",EDGE,"E7");var subQ2=sQuery(id+"F0.wireOp",EDGE,"E6");var subQ3=sQuery(id+"F0.wireOp",EDGE,"E5");var subQ4=sQuery(id+"F0.wireOp",EDGE,"E4");var subQ5=sQuery(id+"F0.wireOp",EDGE,"E1.bottom");var subQ6=sQuery(id+"F0.wireOp",EDGE,"E21.filletArc");var subQ7=sQuery(id+"F0.wireOp",EDGE,"E1.top");var subQ8=sQuery(id+"F0.wireOp",EDGE,"E1.left");var subQ9=sQuery(id+"F0.wireOp",EDGE,"E1.right");var subQ10=sQuery(id+"F0.wireOp",EDGE,"E23.filletArc");var subQ11=sQuery(id+"F0.wireOp",EDGE,"E24.filletArc");Q0=makeQuery(id+"F2.boolean.opBoolean","SPLIT",FACE,{"disambiguationData":[TD([makeQuery(id+"F1.opExtrude","SWEPT_FACE",FACE,{"disambiguationData":[OSD([subQ5])]})])],"derivedFrom":makeQuery(id+"F1.opExtrude","CAP_FACE",FACE,{"disambiguationData":[OSD([subQ5,subQ7,subQ8,subQ9,subQ4,subQ3,subQ2,subQ1,subQ6,subQ0,subQ10,subQ11])],"isStart":true})});}
            var sketch = newSketch(context, id + "F16", { "sketchPlane" : qUnion([Q0])});
            skLineSegment(sketch, "E79", {"start": v(-33, 90) * mm, "end": v(-15, 108) * mm});
            skLineSegment(sketch, "E80", {"start": v(-15, 108) * mm, "end": v(-15, 120) * mm});
            skLineSegment(sketch, "E81", {"start": v(33, 90) * mm, "end": v(15, 108) * mm});
            skLineSegment(sketch, "E82", {"start": v(15, 108) * mm, "end": v(15, 120) * mm});
            skLineSegment(sketch, "E83", {"start": v(-0.1, 90) * mm, "end": v(-0.1, 120) * mm, "construction": true});
            skCircle(sketch, "E84", {"center": v(-0.1, 120) * mm, "radius": 6 * mm});
            skArc(sketch, "E85", {"start": v(15, 120) * mm, "mid": v(0, 135) * mm, "end": v(-15, 120) * mm});
            skLineSegment(sketch, "E86", {"start": v(-70, 90) * mm, "end": v(-33, 90) * mm, "construction": true});
            skLineSegment(sketch, "E87", {"start": v(33, 90) * mm, "end": v(70, 90) * mm, "construction": true});
            skLineSegment(sketch, "E88", {"start": v(0, 0) * mm, "end": v(-80, 0) * mm, "construction": true});
            skLineSegment(sketch, "E89", {"start": v(-80, 0) * mm, "end": v(0, 0) * mm, "construction": true});
            skLineSegment(sketch, "E90", {"start": v(80, 0) * mm, "end": v(0, 0) * mm, "construction": true});
            skLineSegment(sketch, "E91.MirrorCS", {"start": v(15, -108) * mm, "end": v(15, -120) * mm});
            skArc(sketch, "E92.MirrorCS", {"start": v(15, -120) * mm, "mid": v(0, -135) * mm, "end": v(-15, -120) * mm});
            skLineSegment(sketch, "E93.MirrorCS", {"start": v(-15, -108) * mm, "end": v(-15, -120) * mm});
            skCircle(sketch, "E94.MirrorC", {"center": v(-0.1, -120) * mm, "radius": 6 * mm});
            skLineSegment(sketch, "E95.MirrorCS", {"start": v(33, -90) * mm, "end": v(15, -108) * mm});
            skLineSegment(sketch, "E96.MirrorCS", {"start": v(-0.1, -90) * mm, "end": v(-0.1, -120) * mm, "construction": true});
            skLineSegment(sketch, "E97.MirrorCS", {"start": v(-33, -90) * mm, "end": v(-15, -108) * mm});
            skSolve(sketch);
        }
        {
            var Q0;
            {var subQ1=sQuery(id+"F16.wireOp",EDGE,"E79");Q0=makeQuery(id+"F16.imprint","IMPRINT",FACE,{"disambiguationData":[TD([[makeQuery(id+"F16.imprint","IMPRINT",EDGE,{"derivedFrom":subQ1}),-1.0]])]});}
            var Q1;
            Q1=makeQuery(id+"F16.imprint","IMPRINT",FACE,{"disambiguationData":[TD([[makeQuery(id+"F16.imprint","IMPRINT",EDGE,{"derivedFrom":makeQuery(id+"F1.opExtrude","CAP_EDGE",EDGE,{"disambiguationData":[OSD([sQuery(id+"F0.wireOp",EDGE,"E1.left")])],"isStart":true})}),-1.0]])]});
            var Q2;
            {var subQ1=sQuery(id+"F16.wireOp",EDGE,"E97.MirrorCS");Q2=makeQuery(id+"F16.imprint","IMPRINT",FACE,{"disambiguationData":[TD([[makeQuery(id+"F16.imprint","IMPRINT",EDGE,{"derivedFrom":subQ1}),1.0]])]});}
            var Q3;
            Q3=makeQuery(id+"F2.opExtrude","CAP_FACE",FACE,{"disambiguationData":[OSD([sQuery(id+"F0.wireOp",EDGE,"E12"),sQuery(id+"F0.wireOp",EDGE,"E13"),sQuery(id+"F0.wireOp",EDGE,"E14"),sQuery(id+"F0.wireOp",EDGE,"E15"),sQuery(id+"F0.wireOp",EDGE,"E17.filletArc"),sQuery(id+"F0.wireOp",EDGE,"E18.filletArc"),sQuery(id+"F0.wireOp",EDGE,"E19.filletArc"),sQuery(id+"F0.wireOp",EDGE,"E20.filletArc"),sQuery(id+"F0.wireOp",EDGE,"E25.0"),sQuery(id+"F0.wireOp",EDGE,"E25.1"),sQuery(id+"F0.wireOp",EDGE,"E25.2"),sQuery(id+"F0.wireOp",EDGE,"E25.3"),sQuery(id+"F0.wireOp",EDGE,"E25.4"),sQuery(id+"F0.wireOp",EDGE,"E25.5"),sQuery(id+"F0.wireOp",EDGE,"E25.6"),sQuery(id+"F0.wireOp",EDGE,"E25.7")])],"isStart":false});
            extrude(context, id + "F17", {"entities" : qUnion([Q0, Q1, Q2]), "endBound" : BoundingType.UP_TO_SURFACE, "endBoundEntityFace" : qUnion([Q3]), "depth" : 25 * mm});
        }
    });
